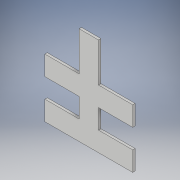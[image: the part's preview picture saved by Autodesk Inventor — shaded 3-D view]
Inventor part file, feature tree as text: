
AUTODESK INVENTOR PART (.ipt)
format: ipt  version: 2017 (Build 210142000, 142)  size: 122,880 bytes
history: native  units: in
note: dims shown in document units (in); Inventor stores cm internally (conversion verified against a paired STEP export)
features: extrude x2, sketch x2, thicken_offset x1
ambient origin geometry x8: Origin, YZ Plane, XZ Plane, XY Plane, X Axis, Y Axis, Z Axis, Center Point
bodies: Solid1 (feature_tree)
feature tree (5):
  extrude  "Extrusion1"  Depth=14.0in
  extrude  "Extrusion3"  Depth=0.25in TaperAngle=0.0deg
  thicken_offset  "Thicken1"
  sketch  "Sketch1"  dims[d0=2.0in d1=14.0in]
  sketch  "Sketch2"  dims[d2=0.25in d3=0.0in d6=0.25in d7=0.0in d8=4.0in d9=4.0in]
